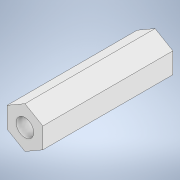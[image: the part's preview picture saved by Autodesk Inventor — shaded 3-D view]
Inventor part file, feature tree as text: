
AUTODESK INVENTOR PART (.ipt)
format: ipt  version: 2022 (Build 260153000, 153)  size: 98,816 bytes
history: native  units: mm
features: other x1, extrude x1, sketch x1
ambient origin geometry x8: Origin, YZ Plane, XZ Plane, XY Plane, X Axis, Y Axis, Z Axis, Center Point
bodies: Body1 (feature_tree)
feature tree (3):
  other  "ソリッド1"
  extrude  "押し出し1"  Depth=5.5mm
  sketch  "スケッチ1"
